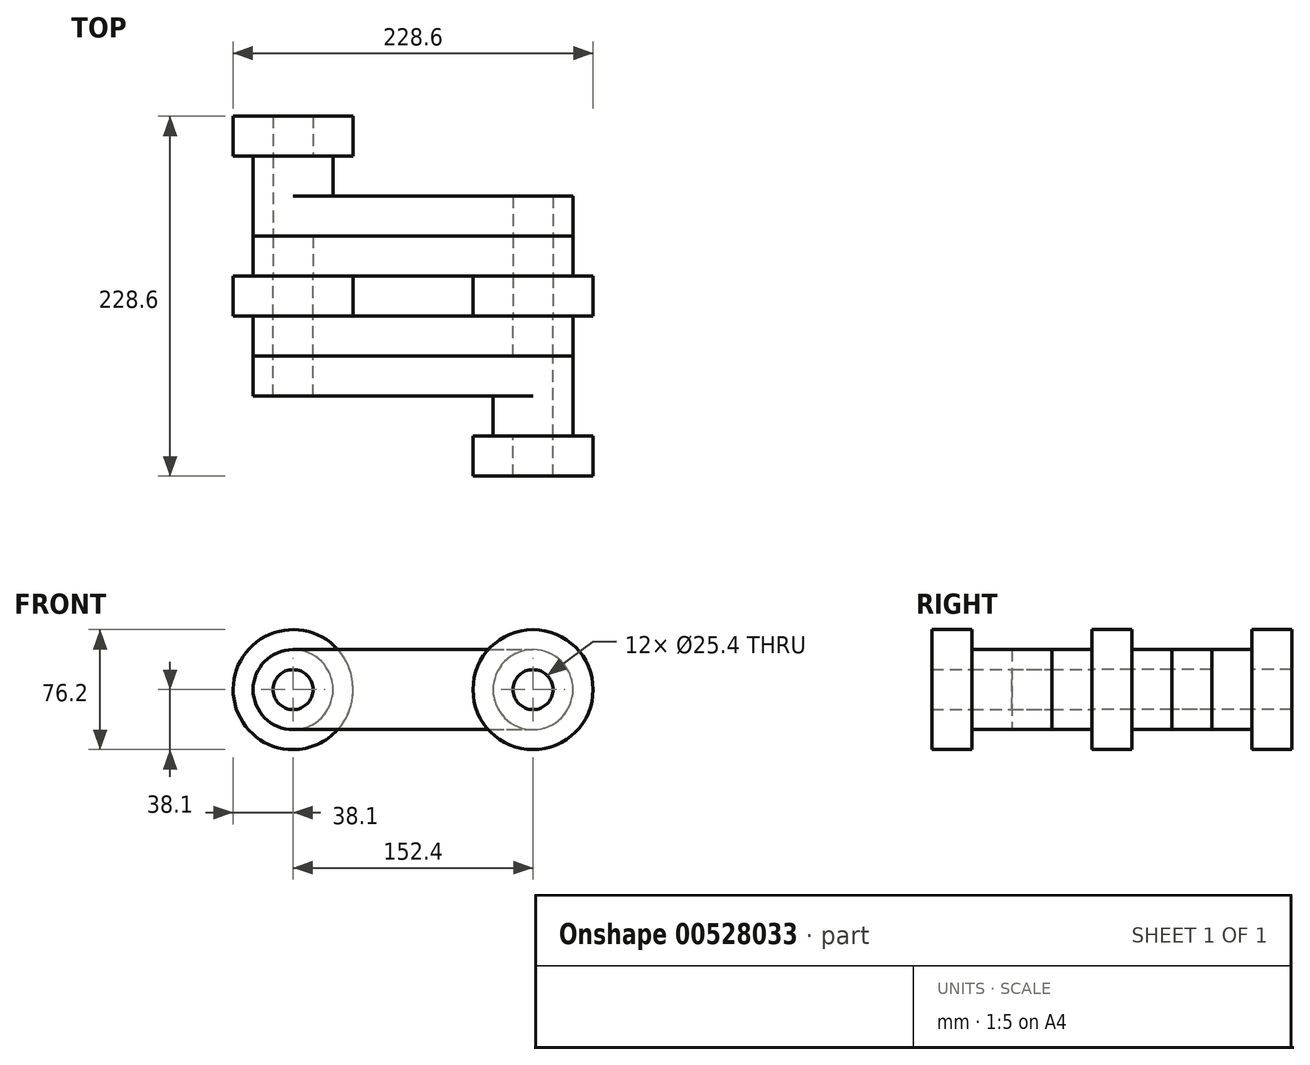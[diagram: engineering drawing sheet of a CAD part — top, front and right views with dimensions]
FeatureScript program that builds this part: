
annotation { "Feature Type Name" : "Feature", "Feature Type Description" : "" }
export const myFeature = defineFeature(function(context is Context, id is Id, definition is map)
    precondition{}
    {
        {
            var Q0;
            Q0=qCreatedBy(makeId("Front.planeOp"),FACE);
            var sketch = newSketch(context, id + "F0", { "sketchPlane" : qUnion([Q0])});
            skCircle(sketch, "E0", {"center": v(-76.2, 0) * mm, "radius": 38.1 * mm, "construction": true});
            skCircle(sketch, "E1", {"center": v(76.2, 0) * mm, "radius": 38.1 * mm});
            skCircle(sketch, "E2", {"center": v(76.2, 0) * mm, "radius": 12.7 * mm});
            skCircle(sketch, "E3", {"center": v(-76.2, 0) * mm, "radius": 12.7 * mm, "construction": true});
            skLineSegment(sketch, "E4", {"start": v(0, 91.23) * mm, "end": v(0, -58.95) * mm, "construction": true});
            skSolve(sketch);
        }
        {
            var Q0;
            Q0 = qSketchRegion(id + "F0", true);
            extrude(context, id + "F1", {"entities" : qUnion([Q0]), "oppositeDirection" : true, "depth" : 25.4 * mm, "offsetDistance" : 25.4 * mm, "symmetric" : true});
        }
        {
            var Q0;
            Q0=makeQuery(id+"F1.opExtrude","CAP_FACE",FACE,{"disambiguationData":[OSD([sQuery(id+"F0.wireOp",EDGE,"E1"),sQuery(id+"F0.wireOp",EDGE,"E2")])],"isStart":true});
            var sketch = newSketch(context, id + "F2", { "sketchPlane" : qUnion([Q0])});
            skCircle(sketch, "E5.0", {"center": v(76.2, 0) * mm, "radius": 12.7 * mm});
            skCircle(sketch, "E5.1", {"center": v(-76.2, 0) * mm, "radius": 12.7 * mm});
            skLineSegment(sketch, "E6", {"start": v(-76.2, 0) * mm, "end": v(76.2, 0) * mm});
            skArc(sketch, "E7.0.startCap", {"start": v(-76.2, -25.4) * mm, "mid": v(-101.6, 0) * mm, "end": v(-76.2, 25.4) * mm});
            skArc(sketch, "E7.0.endCap", {"start": v(76.2, 25.4) * mm, "mid": v(101.6, 0) * mm, "end": v(76.2, -25.4) * mm});
            skLineSegment(sketch, "E7.0.left", {"start": v(-76.2, 25.4) * mm, "end": v(76.2, 25.4) * mm});
            skLineSegment(sketch, "E7.0.right", {"start": v(-76.2, -25.4) * mm, "end": v(76.2, -25.4) * mm});
            skSolve(sketch);
        }
        {
            var Q0;
            Q0 = qSketchRegion(id + "F2", true);
            extrude(context, id + "F3", {"entities" : qUnion([Q0]), "depth" : 25.4 * mm, "offsetDistance" : 25.4 * mm});
        }
        {
            var Q0;
            Q0=makeQuery(id+"F3.opExtrude","CAP_FACE",FACE,{"disambiguationData":[OSD([sQuery(id+"F2.wireOp",EDGE,"E5.0"),sQuery(id+"F2.wireOp",EDGE,"E5.1"),sQuery(id+"F2.wireOp",EDGE,"E7.0.startCap"),sQuery(id+"F2.wireOp",EDGE,"E7.0.endCap"),sQuery(id+"F2.wireOp",EDGE,"E7.0.left"),sQuery(id+"F2.wireOp",EDGE,"E7.0.right")])],"isStart":false});
            var sketch = newSketch(context, id + "F4", { "sketchPlane" : qUnion([Q0])});
            skLineSegment(sketch, "E8.0.0", {"start": v(76.2, 25.4) * mm, "end": v(-76.2, 25.4) * mm});
            skArc(sketch, "E8.0.1", {"start": v(-76.2, 25.4) * mm, "mid": v(-101.6, 0) * mm, "end": v(-76.2, -25.4) * mm});
            skLineSegment(sketch, "E8.0.2", {"start": v(-76.2, -25.4) * mm, "end": v(76.2, -25.4) * mm});
            skArc(sketch, "E8.0.3", {"start": v(76.2, -25.4) * mm, "mid": v(101.6, 0) * mm, "end": v(76.2, 25.4) * mm});
            skCircle(sketch, "E9.0", {"center": v(-76.2, 0) * mm, "radius": 12.7 * mm});
            skCircle(sketch, "E9.1", {"center": v(76.2, 0) * mm, "radius": 12.7 * mm});
            skSolve(sketch);
        }
        {
            var Q0;
            Q0 = qSketchRegion(id + "F4", true);
            extrude(context, id + "F5", {"entities" : qUnion([Q0]), "depth" : 25.4 * mm, "offsetDistance" : 25.4 * mm});
        }
        {
            var Q0;
            Q0=makeQuery(id+"F5.opExtrude","CAP_FACE",FACE,{"disambiguationData":[OSD([sQuery(id+"F4.wireOp",EDGE,"E8.0.0"),sQuery(id+"F4.wireOp",EDGE,"E8.0.1"),sQuery(id+"F4.wireOp",EDGE,"E8.0.2"),sQuery(id+"F4.wireOp",EDGE,"E8.0.3"),sQuery(id+"F4.wireOp",EDGE,"E9.0"),sQuery(id+"F4.wireOp",EDGE,"E9.1")])],"isStart":false});
            var sketch = newSketch(context, id + "F6", { "sketchPlane" : qUnion([Q0])});
            skCircle(sketch, "E10", {"center": v(76.2, 0) * mm, "radius": 25.4 * mm});
            skCircle(sketch, "E11.0", {"center": v(76.2, 0) * mm, "radius": 12.7 * mm});
            skSolve(sketch);
        }
        {
            var Q0;
            Q0 = qSketchRegion(id + "F6", true);
            extrude(context, id + "F7", {"entities" : qUnion([Q0]), "operationType" : NewBodyOperationType.ADD, "depth" : 25.4 * mm, "offsetDistance" : 25.4 * mm});
        }
        {
            var Q0;
            Q0=makeQuery(id+"F7.opExtrude","CAP_FACE",FACE,{"disambiguationData":[OSD([sQuery(id+"F6.wireOp",EDGE,"E10"),sQuery(id+"F6.wireOp",EDGE,"E11.0")])],"isStart":false});
            var sketch = newSketch(context, id + "F8", { "sketchPlane" : qUnion([Q0])});
            skCircle(sketch, "E12.0", {"center": v(76.2, 0) * mm, "radius": 38.1 * mm});
            skCircle(sketch, "E13.0", {"center": v(76.2, 0) * mm, "radius": 12.7 * mm});
            skSolve(sketch);
        }
        {
            var Q0;
            Q0 = qSketchRegion(id + "F8", true);
            extrude(context, id + "F9", {"entities" : qUnion([Q0]), "depth" : 25.4 * mm, "offsetDistance" : 25.4 * mm});
        }
        {
            var Q0;
            Q0=makeQuery(id+"F1.opExtrude","SWEPT_BODY",BODY,{"disambiguationData":[OSD([sQuery(id+"F0.wireOp",EDGE,"E1"),sQuery(id+"F0.wireOp",EDGE,"E2")])]});
            var Q1;
            Q1=makeQuery(id+"F3.opExtrude","SWEPT_BODY",BODY,{"disambiguationData":[OSD([sQuery(id+"F2.wireOp",EDGE,"E5.0"),sQuery(id+"F2.wireOp",EDGE,"E5.1"),sQuery(id+"F2.wireOp",EDGE,"E7.0.startCap"),sQuery(id+"F2.wireOp",EDGE,"E7.0.endCap"),sQuery(id+"F2.wireOp",EDGE,"E7.0.left"),sQuery(id+"F2.wireOp",EDGE,"E7.0.right")])]});
            var Q2;
            Q2=makeQuery(id+"F5.opExtrude","SWEPT_BODY",BODY,{"disambiguationData":[OSD([sQuery(id+"F4.wireOp",EDGE,"E8.0.0"),sQuery(id+"F4.wireOp",EDGE,"E8.0.1"),sQuery(id+"F4.wireOp",EDGE,"E8.0.2"),sQuery(id+"F4.wireOp",EDGE,"E8.0.3"),sQuery(id+"F4.wireOp",EDGE,"E9.0"),sQuery(id+"F4.wireOp",EDGE,"E9.1")])]});
            var Q3;
            Q3=makeQuery(id+"F9.opExtrude","SWEPT_BODY",BODY,{"disambiguationData":[OSD([sQuery(id+"F8.wireOp",EDGE,"E12.0"),sQuery(id+"F8.wireOp",EDGE,"E13.0")])]});
            var Q4;
            Q4=sQuery(id+"F0.wireOp",EDGE,"E4");
            circularPattern(context, id + "F10", {"entities" : qUnion([Q0, Q1, Q2, Q3]), "axis" : qUnion([Q4]), "angle" : 360 * degree, "instanceCount" : 2, "equalSpace" : true, "computeTransformsWithoutBuiltin" : true});
        }
    });
